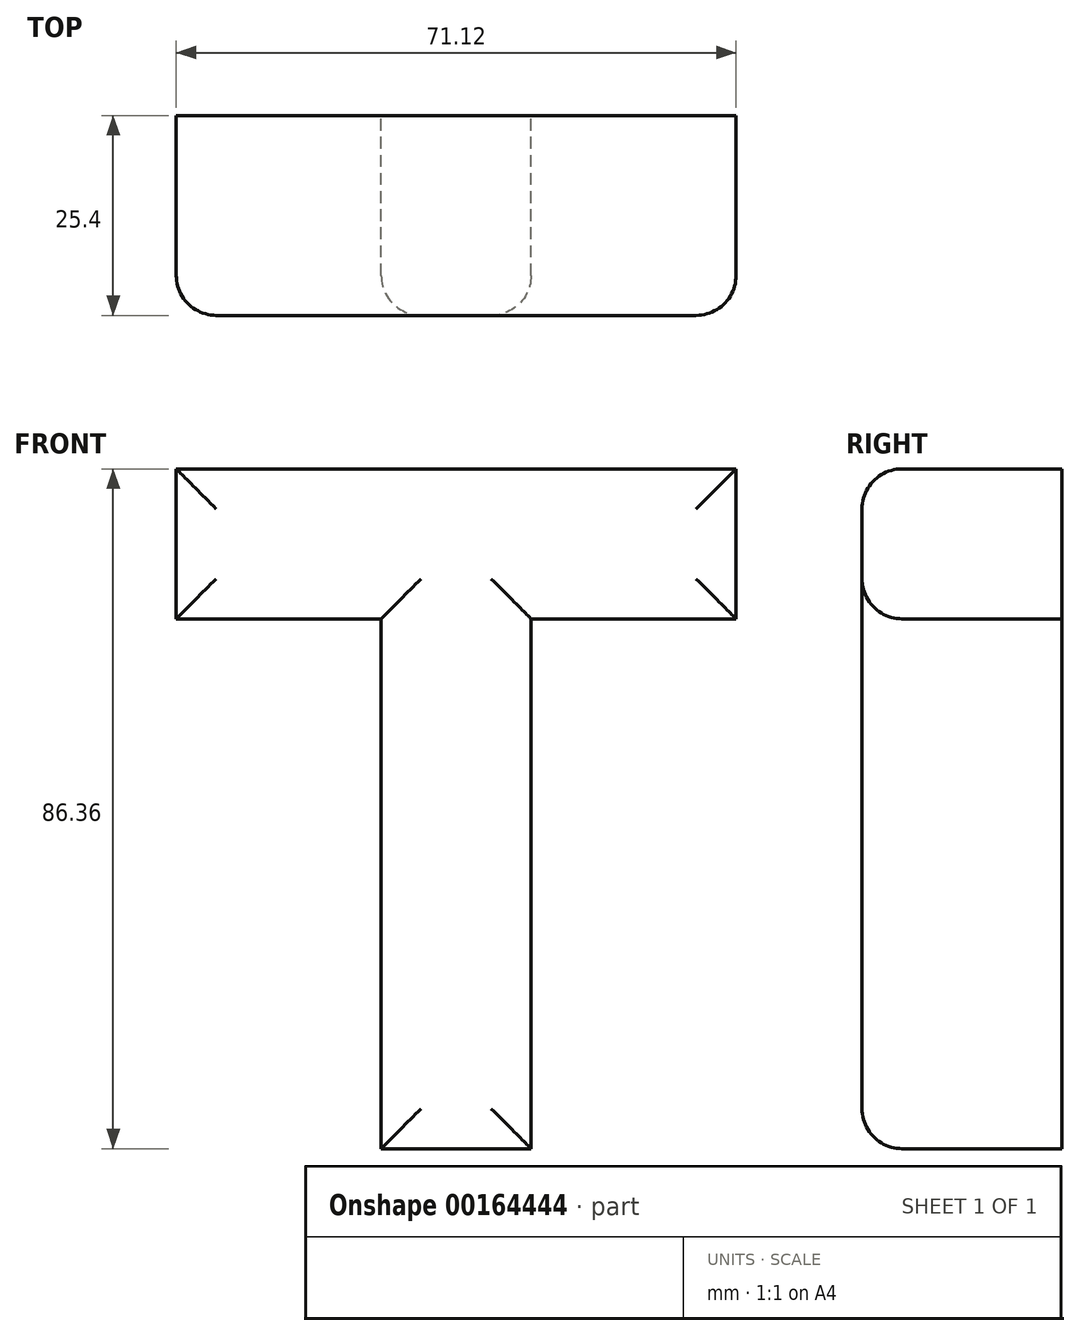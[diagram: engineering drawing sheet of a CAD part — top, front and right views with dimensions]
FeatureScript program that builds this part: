
annotation { "Feature Type Name" : "Feature", "Feature Type Description" : "" }
export const myFeature = defineFeature(function(context is Context, id is Id, definition is map)
    precondition{}
    {
        {
            var Q0;
            Q0=qCreatedBy(makeId("Front.planeOp"),FACE);
            var sketch = newSketch(context, id + "F0", { "sketchPlane" : qUnion([Q0])});
            skLineSegment(sketch, "E0", {"start": v(-35.56, 24.13) * mm, "end": v(-35.56, 43.18) * mm});
            skLineSegment(sketch, "E1", {"start": v(-35.56, 43.18) * mm, "end": v(35.56, 43.18) * mm});
            skLineSegment(sketch, "E2", {"start": v(35.56, 43.18) * mm, "end": v(35.56, 24.13) * mm});
            skLineSegment(sketch, "E3", {"start": v(35.56, 24.13) * mm, "end": v(9.52, 24.13) * mm});
            skLineSegment(sketch, "E4", {"start": v(9.52, 24.13) * mm, "end": v(9.53, -43.18) * mm});
            skLineSegment(sketch, "E5", {"start": v(9.53, -43.18) * mm, "end": v(-9.52, -43.18) * mm});
            skLineSegment(sketch, "E6", {"start": v(-9.52, -43.18) * mm, "end": v(-9.53, 24.13) * mm});
            skLineSegment(sketch, "E7", {"start": v(-9.53, 24.13) * mm, "end": v(-35.56, 24.13) * mm});
            skSolve(sketch);
        }
        {
            var Q0;
            Q0=makeQuery(id+"F0.imprint","IMPRINT",FACE,{"disambiguationData":[TD([[makeQuery(id+"F0.imprint","IMPRINT",EDGE,{"derivedFrom":sQuery(id+"F0.wireOp",EDGE,"E0")}),-1.0]])]});
            extrude(context, id + "F1", {"entities" : qUnion([Q0]), "depth" : 25.4 * mm});
        }
        {
            var Q0;
            Q0=makeQuery(id+"F1.opExtrude","CAP_EDGE",EDGE,{"disambiguationData":[OSD([sQuery(id+"F0.wireOp",EDGE,"E1")])],"isStart":false});
            var Q1;
            Q1=makeQuery(id+"F1.opExtrude","CAP_EDGE",EDGE,{"disambiguationData":[OSD([sQuery(id+"F0.wireOp",EDGE,"E2")])],"isStart":false});
            var Q2;
            Q2=makeQuery(id+"F1.opExtrude","CAP_EDGE",EDGE,{"disambiguationData":[OSD([sQuery(id+"F0.wireOp",EDGE,"E3")])],"isStart":false});
            var Q3;
            Q3=makeQuery(id+"F1.opExtrude","CAP_EDGE",EDGE,{"disambiguationData":[OSD([sQuery(id+"F0.wireOp",EDGE,"E4")])],"isStart":false});
            var Q4;
            Q4=makeQuery(id+"F1.opExtrude","CAP_EDGE",EDGE,{"disambiguationData":[OSD([sQuery(id+"F0.wireOp",EDGE,"E5")])],"isStart":false});
            var Q5;
            Q5=makeQuery(id+"F1.opExtrude","CAP_EDGE",EDGE,{"disambiguationData":[OSD([sQuery(id+"F0.wireOp",EDGE,"E6")])],"isStart":false});
            var Q6;
            Q6=makeQuery(id+"F1.opExtrude","CAP_EDGE",EDGE,{"disambiguationData":[OSD([sQuery(id+"F0.wireOp",EDGE,"E7")])],"isStart":false});
            var Q7;
            Q7=makeQuery(id+"F1.opExtrude","CAP_EDGE",EDGE,{"disambiguationData":[OSD([sQuery(id+"F0.wireOp",EDGE,"E0")])],"isStart":false});
            fillet(context, id + "F2", {"entities" : qUnion([Q0, Q1, Q2, Q3, Q4, Q5, Q6, Q7]), "radius" : 5.08 * mm, "tangentPropagation" : true, "allowEdgeOverflow" : false});
        }
    });
